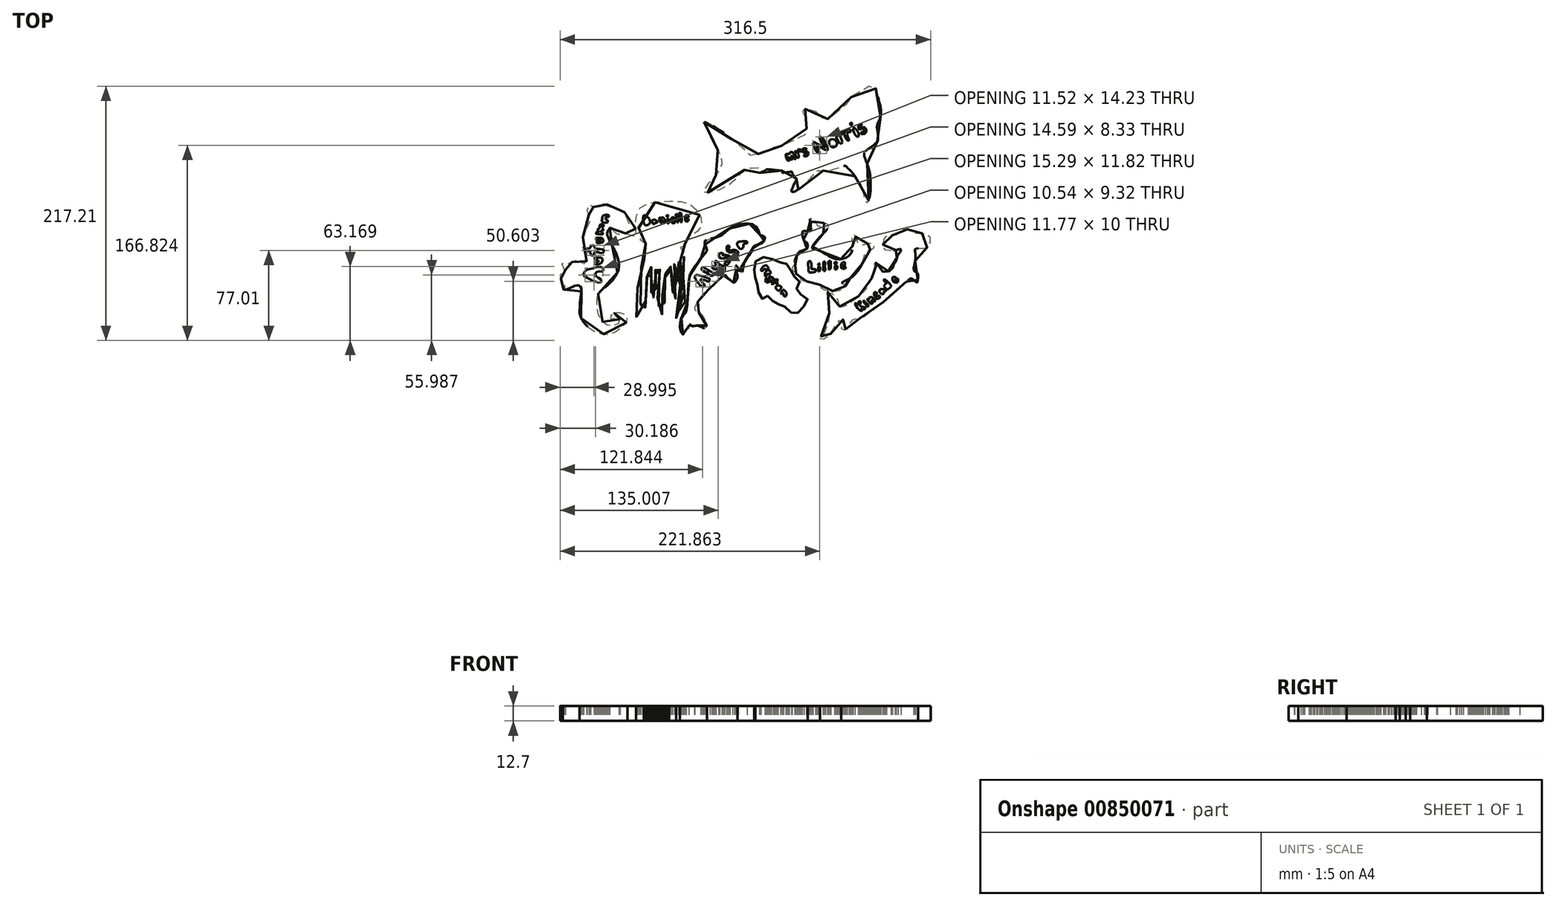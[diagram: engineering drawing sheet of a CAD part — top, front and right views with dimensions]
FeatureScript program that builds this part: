
annotation { "Feature Type Name" : "Feature", "Feature Type Description" : "" }
export const myFeature = defineFeature(function(context is Context, id is Id, definition is map)
    precondition{}
    {
        {
            var Q0;
            Q0=qCreatedBy(makeId("Top.planeOp"),FACE);
            var sketch = newSketch(context, id + "F0", { "sketchPlane" : qUnion([Q0])});
            skFitSpline(sketch, "E0", {"points": [v(-59.86, -6.15) * mm, v(-60.63, -4.76) * mm, v(-62.85, -4.35) * mm, v(-64.45, -3.65) * mm, v(-64.24, -1.7) * mm, v(-62.57, 0) * mm, v(-63.47, 2.6) * mm, v(-65.98, 7.6) * mm, v(-68.13, 12.13) * mm, v(-68.27, 15.81) * mm, v(-64.02, 25.07) * mm, v(-53.18, 29.24) * mm, v(-34.55, 30.36) * mm, v(-21.77, 27.58) * mm, v(-13.98, 18.68) * mm, v(-11.76, 10.34) * mm, v(-16.76, 3.39) * mm, v(-25.94, -2.17) * mm, v(-26.21, -5.5) * mm, v(-28.44, -8.57) * mm, v(-30.38, -9.12) * mm, v(-27.6, -11.9) * mm, v(-27.88, -14.68) * mm, v(-27.05, -18.3) * mm, v(-30.1, -19.97) * mm, v(-28.44, -25.8) * mm, v(-27.05, -32.2) * mm, v(-28.16, -37.76) * mm, v(-25.94, -43.87) * mm, v(-27.05, -48.32) * mm, v(-26.21, -54.72) * mm, v(-28.72, -61.95) * mm, v(-30.94, -67.78) * mm, v(-33.72, -70.56) * mm, v(-32.05, -62.22) * mm, v(-29.83, -57.22) * mm, v(-30.38, -50.27) * mm, v(-29, -44.7) * mm, v(-31.22, -38.04) * mm, v(-30.1, -34.14) * mm, v(-31.5, -28.58) * mm, v(-32.33, -20.52) * mm, v(-34.83, -20.8) * mm, v(-34, -29.97) * mm, v(-32.05, -34.14) * mm, v(-33.72, -38.04) * mm, v(-32.05, -45.26) * mm, v(-35.67, -54.16) * mm, v(-37.33, -43.6) * mm, v(-39.84, -36.92) * mm, v(-37.06, -32.2) * mm, v(-38.45, -26.92) * mm, v(-38.72, -21.08) * mm, v(-42.62, -21.08) * mm, v(-41.96, -25.83) * mm, v(-42.72, -30.28) * mm, v(-43.28, -36.53) * mm, v(-42.65, -40.84) * mm, v(-43.35, -44.6) * mm, v(-45.3, -48.35) * mm, v(-45.7, -51.75) * mm, v(-44.18, -55.16) * mm, v(-43.83, -59.12) * mm, v(-45.36, -61.13) * mm, v(-45.78, -66.83) * mm, v(-45.7, -67.53) * mm, v(-47.93, -65.24) * mm, v(-48.07, -61) * mm, v(-49.6, -57.1) * mm, v(-49.25, -50.78) * mm, v(-47.38, -43.97) * mm, v(-48.21, -34.86) * mm, v(-47.52, -27.63) * mm, v(-45.7, -22.35) * mm, v(-48.7, -21.17) * mm, v(-48.7, -24.5) * mm, v(-51.27, -27.56) * mm, v(-51.69, -30.9) * mm, v(-50.64, -33.4) * mm, v(-52.03, -37.02) * mm, v(-52.1, -39.24) * mm, v(-50.92, -44.1) * mm, v(-52.94, -48.14) * mm, v(-53.35, -51.54) * mm, v(-53.63, -53.9) * mm, v(-55.65, -50.08) * mm, v(-55.02, -47.51) * mm, v(-57.18, -43.06) * mm, v(-55.16, -35.14) * mm, v(-55.79, -29.72) * mm, v(-54.81, -20.68) * mm, v(-57.32, -20.06) * mm, v(-58.5, -28.05) * mm, v(-58.85, -34.65) * mm, v(-60.37, -40.77) * mm, v(-61.28, -45.08) * mm, v(-59.96, -49.11) * mm, v(-59.89, -56.48) * mm, v(-60.93, -63.64) * mm, v(-63.5, -67.39) * mm, v(-67.17, -71.06) * mm, v(-66.98, -61.23) * mm, v(-64.42, -58.28) * mm, v(-66.2, -47.08) * mm, v(-66.39, -42.56) * mm, v(-64.03, -37.64) * mm, v(-63.83, -27.42) * mm, v(-61.28, -18.18) * mm, v(-65.6, -15.62) * mm, v(-64.42, -11.89) * mm, v(-65.01, -9.53) * mm, v(-59.86, -6.15) * mm]});
            skFitSpline(sketch, "E1", {"points": [v(-60.84, 10.3) * mm, v(-61.48, 18.1) * mm, v(-58.93, 17.3) * mm, v(-56.22, 13.96) * mm, v(-57.01, 10.45) * mm, v(-58.77, 9.81) * mm, v(-60.84, 10.3) * mm]});
            skFitSpline(sketch, "E2", {"points": [v(-52.86, 10.57) * mm, v(-54.3, 13.64) * mm, v(-52.87, 14.6) * mm, v(-51.12, 13.96) * mm, v(-50, 12.52) * mm, v(-50.5, 11.76) * mm, v(-51.63, 11.9) * mm, v(-52.86, 10.57) * mm]});
            skFitSpline(sketch, "E3", {"points": [v(-47.61, 12.36) * mm, v(-48.09, 16.19) * mm, v(-47.13, 16.19) * mm, v(-46.97, 15.4) * mm, v(-45.7, 16.5) * mm, v(-44.1, 15.4) * mm, v(-43.3, 12.84) * mm, v(-44.42, 12.2) * mm, v(-45.22, 13.8) * mm, v(-46.34, 13.96) * mm, v(-46.04, 12.16) * mm, v(-47.61, 12.36) * mm]});
            skFitSpline(sketch, "E4", {"points": [v(-40.96, 11.48) * mm, v(-41.41, 15.2) * mm, v(-40.4, 15.32) * mm, v(-40.23, 11.6) * mm, v(-40.96, 11.48) * mm]});
            skFitSpline(sketch, "E5", {"points": [v(-41.19, 17.06) * mm, v(-42.03, 17.46) * mm, v(-41.41, 18.36) * mm, v(-40.51, 17.9) * mm, v(-41.19, 17.06) * mm]});
            skFitSpline(sketch, "E6", {"points": [v(-36.8, 14.47) * mm, v(-35.33, 15.26) * mm, v(-36.68, 16.67) * mm, v(-38.15, 15.09) * mm, v(-37.75, 12.22) * mm, v(-35.27, 11.65) * mm, v(-35.05, 13.12) * mm, v(-36.74, 12.9) * mm, v(-36.8, 14.47) * mm]});
            skFitSpline(sketch, "E7", {"points": [v(-33.07, 12.44) * mm, v(-34.09, 18.98) * mm, v(-32.9, 18.98) * mm, v(-32.29, 12.55) * mm, v(-33.07, 12.44) * mm]});
            skFitSpline(sketch, "E8", {"points": [v(-29.98, 12.5) * mm, v(-31.33, 19.94) * mm, v(-29.92, 20.27) * mm, v(-29.24, 16.39) * mm, v(-29.02, 12.67) * mm, v(-29.98, 12.5) * mm]});
            skFitSpline(sketch, "E9", {"points": [v(-24, 15.43) * mm, v(-24.4, 14.53) * mm, v(-25.19, 14.7) * mm, v(-25.13, 15.77) * mm, v(-24.34, 16.16) * mm, v(-23.04, 17.12) * mm, v(-24.23, 18.53) * mm, v(-25.97, 17.9) * mm, v(-26.26, 16.16) * mm, v(-26.09, 13.96) * mm, v(-24.45, 12.9) * mm, v(-23.44, 13.85) * mm, v(-23.21, 15.09) * mm, v(-24, 15.43) * mm]});
            skFitSpline(sketch, "E10", {"points": [v(-76.91, 2.77) * mm, v(-70.73, -0.55) * mm, v(-67.44, 0.8) * mm, v(-66.9, 3.47) * mm, v(-68.38, 6.96) * mm, v(-72.8, 8.37) * mm, v(-73.88, 10.44) * mm, v(-75.62, 14.93) * mm, v(-78.23, 21.03) * mm, v(-79.9, 21.43) * mm, v(-81.72, 22.5) * mm, v(-92.04, 25.05) * mm, v(-92.17, 25.99) * mm, v(-93.72, 28.05) * mm, v(-95.45, 27.44) * mm, v(-96.45, 28.31) * mm, v(-97.73, 29.52) * mm, v(-103.62, 24.9) * mm, v(-104.9, 25.63) * mm, v(-107.64, 27.44) * mm, v(-108.25, 26.3) * mm, v(-107.44, 23.49) * mm, v(-109.79, 22.75) * mm, v(-107.1, 15.45) * mm, v(-108.78, 11.36) * mm, v(-112.47, 2.51) * mm, v(-113.54, 0) * mm, v(-114.08, -8.68) * mm, v(-112, -15.31) * mm, v(-110.37, -20.12) * mm, v(-111.13, -22.06) * mm, v(-113.26, -23.77) * mm, v(-117.62, -21.97) * mm, v(-120.27, -20.03) * mm, v(-122.6, -21.54) * mm, v(-127.38, -22.82) * mm, v(-130.56, -21.92) * mm, v(-131.74, -22.87) * mm, v(-129.28, -27.23) * mm, v(-128.47, -28.98) * mm, v(-130.27, -29.79) * mm, v(-132.36, -30.07) * mm, v(-132.8, -32.58) * mm, v(-131.31, -34.15) * mm, v(-131.79, -35.52) * mm, v(-132.8, -36.47) * mm, v(-132.45, -38.8) * mm, v(-129.13, -41.16) * mm, v(-129.47, -42.44) * mm, v(-130.7, -44.05) * mm, v(-129.99, -45.28) * mm, v(-124.25, -43.67) * mm, v(-118.28, -41.54) * mm, v(-115.16, -43.3) * mm, v(-115.53, -51.73) * mm, v(-116.06, -59.3) * mm, v(-116.06, -66.6) * mm, v(-113.12, -72.67) * mm, v(-106.1, -79.54) * mm, v(-97.48, -83.1) * mm, v(-89, -83.05) * mm, v(-82.8, -79.16) * mm, v(-77, -73.95) * mm, v(-75.5, -70.59) * mm, v(-76.35, -67.46) * mm, v(-81.27, -65.28) * mm, v(-86.3, -65.09) * mm, v(-89.38, -67.41) * mm, v(-90.42, -70.16) * mm, v(-86.63, -69.73) * mm, v(-83.74, -69.21) * mm, v(-81.9, -71.53) * mm, v(-84.4, -74.9) * mm, v(-89.05, -76.37) * mm, v(-95.2, -74.24) * mm, v(-100.23, -66.37) * mm, v(-101.56, -57.22) * mm, v(-100.56, -49.03) * mm, v(-94.26, -43) * mm, v(-87.24, -36.18) * mm, v(-82.93, -27.47) * mm, v(-83.36, -19.22) * mm, v(-86.44, -11.6) * mm, v(-90.23, -4.44) * mm, v(-92.32, 0.54) * mm, v(-92.79, 3.15) * mm, v(-91.46, 6.23) * mm, v(-90.14, 7.65) * mm, v(-87.72, 5.75) * mm, v(-85.3, 3) * mm, v(-79.9, 2.3) * mm, v(-76.91, 2.77) * mm]});
            skFitSpline(sketch, "E11", {"points": [v(-97.57, 12.86) * mm, v(-95.35, 12.15) * mm, v(-93.36, 11.96) * mm, v(-92.46, 12.43) * mm, v(-92.08, 13.48) * mm, v(-93.12, 14.28) * mm, v(-94.02, 14.85) * mm, v(-94.21, 15.85) * mm, v(-93.83, 16.56) * mm, v(-93.26, 16.8) * mm, v(-92.22, 16.84) * mm, v(-91.7, 16.84) * mm, v(-91.27, 17.36) * mm, v(-91.32, 18.26) * mm, v(-92.36, 18.5) * mm, v(-94.3, 18.5) * mm, v(-95.58, 18.07) * mm, v(-96.4, 17.79) * mm, v(-96.96, 16.46) * mm, v(-96.96, 15.23) * mm, v(-97.43, 13.95) * mm, v(-97.57, 12.86) * mm]});
            skFitSpline(sketch, "E12", {"points": [v(-96.25, 6.89) * mm, v(-96.63, 7.74) * mm, v(-97.24, 7.98) * mm, v(-97.2, 8.55) * mm, v(-96.72, 8.93) * mm, v(-96.2, 8.93) * mm, v(-95.82, 8.88) * mm, v(-95.54, 9.26) * mm, v(-95.44, 9.97) * mm, v(-95.68, 10.25) * mm, v(-97.3, 10.54) * mm, v(-98.95, 10.2) * mm, v(-99.28, 8.26) * mm, v(-99.23, 7.27) * mm, v(-100.09, 6.84) * mm, v(-100.9, 6.32) * mm, v(-101.03, 5.52) * mm, v(-100.37, 4.62) * mm, v(-100, 4.14) * mm, v(-100.84, 3.86) * mm, v(-101.84, 4) * mm, v(-102.17, 3.62) * mm, v(-102.31, 2.9) * mm, v(-102.03, 2.39) * mm, v(-100.7, 2.06) * mm, v(-99.85, 2) * mm, v(-98.71, 2) * mm, v(-98.14, 1.96) * mm, v(-96.4, 1.91) * mm, v(-96.44, 3.24) * mm, v(-97, 3.8) * mm, v(-98.2, 4.28) * mm, v(-98.33, 4.76) * mm, v(-97.62, 5.28) * mm, v(-96.3, 5.14) * mm, v(-95.87, 6.23) * mm, v(-96.25, 6.89) * mm]});
            skFitSpline(sketch, "E13", {"points": [v(-101.98, -1.07) * mm, v(-99.23, -1.12) * mm, v(-97.39, -1.17) * mm, v(-96.2, -2.3) * mm, v(-96.06, -3.72) * mm, v(-97.05, -4.96) * mm, v(-98.66, -5.38) * mm, v(-100.56, -5.57) * mm, v(-101.32, -5.53) * mm, v(-101.7, -4.44) * mm, v(-101.08, -3.72) * mm, v(-99.38, -3.72) * mm, v(-98.29, -3.58) * mm, v(-98, -2.97) * mm, v(-98.29, -2.78) * mm, v(-99.94, -2.63) * mm, v(-101.18, -2.73) * mm, v(-102.12, -3.06) * mm, v(-102.46, -2.16) * mm, v(-101.98, -1.07) * mm]});
            skFitSpline(sketch, "E14", {"points": [v(-104.02, -15.86) * mm, v(-103.92, -14.24) * mm, v(-103.5, -13.1) * mm, v(-101.65, -13.25) * mm, v(-99.75, -13.58) * mm, v(-97.48, -14) * mm, v(-96.44, -13.77) * mm, v(-95.58, -12.92) * mm, v(-95.58, -11.92) * mm, v(-96.2, -10.97) * mm, v(-99.23, -10.55) * mm, v(-100.99, -10.4) * mm, v(-102.98, -10.12) * mm, v(-103.78, -8.89) * mm, v(-103.64, -7.66) * mm, v(-105.1, -7.47) * mm, v(-106.67, -7.37) * mm, v(-107.24, -8.89) * mm, v(-107, -9.7) * mm, v(-108.05, -10.17) * mm, v(-109.33, -9.93) * mm, v(-110.27, -9.98) * mm, v(-110.32, -11.07) * mm, v(-109.66, -12.2) * mm, v(-108.85, -12.59) * mm, v(-107.57, -12.54) * mm, v(-106.96, -12.59) * mm, v(-106.96, -13.63) * mm, v(-107.05, -14.72) * mm, v(-107, -15.57) * mm, v(-105.96, -16.05) * mm, v(-104.02, -15.86) * mm]});
            skFitSpline(sketch, "E15", {"points": [v(-103.12, -19.84) * mm, v(-101.7, -20.07) * mm, v(-100.42, -20.17) * mm, v(-100.32, -20.69) * mm, v(-100.42, -21.5) * mm, v(-101.5, -21.64) * mm, v(-102.65, -21.83) * mm, v(-103.02, -22.2) * mm, v(-102.98, -23.01) * mm, v(-102.17, -23.58) * mm, v(-100.23, -23.72) * mm, v(-98.43, -22.96) * mm, v(-97.48, -22.06) * mm, v(-96.86, -21.02) * mm, v(-96.67, -19.6) * mm, v(-97, -18.7) * mm, v(-97.62, -17.99) * mm, v(-98.85, -17.9) * mm, v(-101.03, -17.9) * mm, v(-101.93, -17.99) * mm, v(-103.07, -18.04) * mm, v(-103.6, -18.6) * mm, v(-103.5, -19.5) * mm, v(-103.12, -19.84) * mm]});
            skFitSpline(sketch, "E16", {"points": [v(-102.27, -33.86) * mm, v(-103.17, -32.68) * mm, v(-102.98, -31.4) * mm, v(-102.08, -30.5) * mm, v(-100.6, -29.74) * mm, v(-98.85, -29.79) * mm, v(-97.3, -29.83) * mm, v(-96.58, -29.64) * mm, v(-96.01, -28.6) * mm, v(-96.01, -27.6) * mm, v(-96.96, -26.66) * mm, v(-97.86, -26.1) * mm, v(-99.8, -25.8) * mm, v(-102.83, -26.56) * mm, v(-105.82, -27.23) * mm, v(-108.05, -27.7) * mm, v(-108.85, -27.84) * mm, v(-110.04, -28.22) * mm, v(-111.27, -29.36) * mm, v(-112.5, -30.36) * mm, v(-112.88, -31.5) * mm, v(-112.83, -32.91) * mm, v(-111.32, -34.53) * mm, v(-109.56, -35.28) * mm, v(-108.05, -36.23) * mm, v(-105.1, -37.7) * mm, v(-102.93, -38.27) * mm, v(-101.32, -39.07) * mm, v(-99.9, -39.26) * mm, v(-98.48, -39.26) * mm, v(-97.67, -38.17) * mm, v(-98, -36.8) * mm, v(-99.66, -35.38) * mm, v(-101.89, -34.34) * mm, v(-102.27, -33.86) * mm]});
            skFitSpline(sketch, "E17", {"points": [v(-28.23, -83.72) * mm, v(-30.3, -79.34) * mm, v(-30.38, -72.96) * mm, v(-28.4, -67.78) * mm, v(-25.68, -64.75) * mm, v(-24.57, -59.26) * mm, v(-23.45, -44.27) * mm, v(-22.17, -32.96) * mm, v(-18.67, -26.9) * mm, v(-12.77, -18.61) * mm, v(-7.6, -12.4) * mm, v(-7.6, -11.12) * mm, v(-8.55, -8.01) * mm, v(-9.66, -4.35) * mm, v(-8.79, -3.47) * mm, v(-4.8, -1.96) * mm, v(3.09, 0) * mm, v(5.48, 1.4) * mm, v(9.54, 5.3) * mm, v(17.11, 9.84) * mm, v(24.92, 11.2) * mm, v(32.42, 10.4) * mm, v(35.28, 7.29) * mm, v(37.68, 2.19) * mm, v(37.91, 1.07) * mm, v(39.83, 0.91) * mm, v(41.74, 0) * mm, v(42.06, -2.12) * mm, v(40.54, -4.5) * mm, v(37.52, -6.66) * mm, v(33.37, -7.22) * mm, v(31.38, -10.64) * mm, v(27.95, -16.54) * mm, v(25.16, -19.97) * mm, v(24.05, -23.31) * mm, v(22.85, -29.6) * mm, v(22.3, -30.49) * mm, v(21.1, -30) * mm, v(18, -25.3) * mm, v(17.03, -24.59) * mm, v(16.24, -25.62) * mm, v(16.4, -27.22) * mm, v(18.39, -32.24) * mm, v(18.39, -35.35) * mm, v(15.84, -39.07) * mm, v(14.88, -39.07) * mm, v(12.1, -36.7) * mm, v(9.46, -34.23) * mm, v(7.71, -32.8) * mm, v(3.89, -35.75) * mm, v(-2.49, -41.24) * mm, v(-8.15, -47.06) * mm, v(-11.5, -49.77) * mm, v(-14.68, -54.4) * mm, v(-17.23, -58.62) * mm, v(-18.19, -61.8) * mm, v(-16.44, -64.04) * mm, v(-12.7, -66.03) * mm, v(-9.1, -71.05) * mm, v(-7.9, -74.8) * mm, v(-7.75, -77.03) * mm, v(-9.34, -78.14) * mm, v(-12.13, -77.27) * mm, v(-14.28, -76.39) * mm, v(-16.28, -76) * mm, v(-19.07, -76.47) * mm, v(-20.26, -76.47) * mm, v(-22.1, -74.96) * mm, v(-22.9, -76) * mm, v(-23.6, -78.7) * mm, v(-25.52, -79.66) * mm, v(-26.88, -81.49) * mm, v(-28.23, -83.72) * mm]});
            skFitSpline(sketch, "E18", {"points": [v(-10.9, -43.1) * mm, v(-17.6, -35.53) * mm, v(-17.8, -33.98) * mm, v(-16.93, -33.05) * mm, v(-16.13, -32.64) * mm, v(-5.14, -36.33) * mm, v(-5.2, -37.2) * mm, v(-5.68, -38.07) * mm, v(-6.68, -38.34) * mm, v(-12.31, -36.2) * mm, v(-12.98, -36.8) * mm, v(-12.38, -38.2) * mm, v(-10.3, -40.42) * mm, v(-9.36, -41.82) * mm, v(-10.9, -43.1) * mm]});
            skFitSpline(sketch, "E19", {"points": [v(-2.93, -33.58) * mm, v(-7.55, -31.1) * mm, v(-12.1, -28.02) * mm, v(-11.7, -26.48) * mm, v(-11.1, -26.08) * mm, v(-6.15, -28.9) * mm, v(-2, -31.57) * mm, v(-2.33, -32.71) * mm, v(-2.93, -33.58) * mm]});
            skFitSpline(sketch, "E20", {"points": [v(-3.26, -26.55) * mm, v(-1.39, -27.68) * mm, v(0, -28.15) * mm, v(2.23, -26.34) * mm, v(2.77, -25.2) * mm, v(5.31, -26.68) * mm, v(5.25, -28.29) * mm, v(4.04, -29.1) * mm, v(3.24, -29.96) * mm, v(4.3, -31.1) * mm, v(6.19, -30.7) * mm, v(7.4, -29.1) * mm, v(7.6, -25.88) * mm, v(4.04, -24.33) * mm, v(0.9, -20.85) * mm, v(0, -20.65) * mm, v(-0.92, -22.26) * mm, v(0, -23.46) * mm, v(0, -24.8) * mm, v(-1.25, -25.74) * mm, v(-2.8, -24.94) * mm, v(-3.26, -26.55) * mm]});
            skFitSpline(sketch, "E21", {"points": [v(6.39, -14.75) * mm, v(5.72, -15.96) * mm, v(7.06, -15.76) * mm, v(9.34, -15.62) * mm, v(11.68, -16.36) * mm, v(12.28, -18.57) * mm, v(11.81, -21.32) * mm, v(9.74, -24.33) * mm, v(8.06, -24.33) * mm, v(7.73, -22.19) * mm, v(9.54, -21.25) * mm, v(10.27, -18.64) * mm, v(9.27, -17.3) * mm, v(7.4, -18.37) * mm, v(4.71, -18.7) * mm, v(2.77, -17.36) * mm, v(2.77, -14.95) * mm, v(4.91, -13.81) * mm, v(6.39, -14.75) * mm]});
            skFitSpline(sketch, "E22", {"points": [v(11.88, -8.12) * mm, v(11.08, -10) * mm, v(11.35, -11.47) * mm, v(13.42, -11.6) * mm, v(15.5, -11.07) * mm, v(18.25, -12) * mm, v(18.99, -14.75) * mm, v(16.9, -17.3) * mm, v(14.96, -17.83) * mm, v(14.5, -16.3) * mm, v(15.77, -14.88) * mm, v(16.64, -13.48) * mm, v(15.43, -12.8) * mm, v(13.36, -13.41) * mm, v(10.27, -13.08) * mm, v(9.27, -10.2) * mm, v(9.74, -7.71) * mm, v(11.88, -8.12) * mm]});
            skFitSpline(sketch, "E23", {"points": [v(21.46, -10.66) * mm, v(23.4, -8.99) * mm, v(23.94, -6.3) * mm, v(25.35, -5.9) * mm, v(26.83, -5.5) * mm, v(26.42, -4.16) * mm, v(22.67, -4.03) * mm, v(19.39, -4.43) * mm, v(18.25, -6.1) * mm, v(19.05, -8.45) * mm, v(21.46, -10.66) * mm]});
            skFitSpline(sketch, "E24", {"points": [v(44.3, -50.42) * mm, v(42.5, -52.56) * mm, v(39.22, -52.8) * mm, v(36.97, -50.2) * mm, v(36.3, -44.68) * mm, v(35.28, -40.05) * mm, v(34.04, -38.14) * mm, v(33.81, -34.23) * mm, v(32.91, -29.35) * mm, v(33.02, -24.33) * mm, v(35.17, -19.54) * mm, v(41.25, -17.4) * mm, v(46.21, -18.3) * mm, v(52.3, -20.78) * mm, v(55.9, -22.13) * mm, v(58.27, -22.13) * mm, v(62.1, -25.2) * mm, v(64.36, -28.9) * mm, v(65.03, -31.26) * mm, v(67.62, -34.23) * mm, v(71.12, -36.7) * mm, v(71.23, -41.07) * mm, v(69.1, -44.56) * mm, v(69.43, -46.6) * mm, v(74.16, -50.04) * mm, v(78, -52.8) * mm, v(78.1, -55.6) * mm, v(74.27, -60.8) * mm, v(70.44, -64.74) * mm, v(67.62, -66.43) * mm, v(63, -63.72) * mm, v(59.28, -60.57) * mm, v(56.24, -57.1) * mm, v(52.86, -58.09) * mm, v(49.37, -56.17) * mm, v(47.56, -52.68) * mm, v(44.3, -50.42) * mm]});
            skFitSpline(sketch, "E25", {"points": [v(38.55, -28.45) * mm, v(42.76, -24.33) * mm, v(44.28, -25.62) * mm, v(45.07, -27.43) * mm, v(43.04, -28.05) * mm, v(41.4, -27.6) * mm, v(39.77, -29.12) * mm, v(38.55, -28.45) * mm]});
            skFitSpline(sketch, "E26", {"points": [v(42.2, -33.63) * mm, v(42.08, -31.55) * mm, v(42.76, -29.69) * mm, v(44.16, -28.73) * mm, v(46.02, -29.18) * mm, v(46.87, -30.7) * mm, v(46.36, -31.94) * mm, v(44.78, -31.77) * mm, v(43.88, -31.71) * mm, v(43.54, -32.22) * mm, v(43.71, -33.12) * mm, v(43.15, -33.97) * mm, v(42.2, -33.63) * mm]});
            skFitSpline(sketch, "E27", {"points": [v(47.04, -33.52) * mm, v(46.93, -34.42) * mm, v(47.43, -35.1) * mm, v(48.1, -34.76) * mm, v(48.73, -34.81) * mm, v(48.9, -35.43) * mm, v(48.79, -36.4) * mm, v(46.87, -37.91) * mm, v(45.3, -38.93) * mm, v(43.49, -39.04) * mm, v(42.53, -38.3) * mm, v(42.47, -36.62) * mm, v(43.04, -35.77) * mm, v(43.94, -35.77) * mm, v(44.1, -36.62) * mm, v(44.28, -37.58) * mm, v(45.46, -37.18) * mm, v(46.08, -36.56) * mm, v(46.02, -35.72) * mm, v(45.46, -35.38) * mm, v(45.35, -34.48) * mm, v(47.04, -33.52) * mm]});
            skFitSpline(sketch, "E28", {"points": [v(47.43, -40) * mm, v(48.73, -39.1) * mm, v(50.08, -38.3) * mm, v(49.3, -36.9) * mm, v(50.03, -36.17) * mm, v(51.15, -37.01) * mm, v(52.34, -36.34) * mm, v(53.07, -37.07) * mm, v(52, -37.97) * mm, v(52.45, -38.87) * mm, v(52.9, -39.6) * mm, v(52.11, -40.11) * mm, v(51.1, -39.6) * mm, v(50.53, -39.1) * mm, v(50.2, -39.6) * mm, v(48.5, -40.56) * mm, v(47.43, -40) * mm]});
            skFitSpline(sketch, "E29", {"points": [v(51.94, -45.07) * mm, v(51.43, -42.87) * mm, v(53.12, -41.63) * mm, v(54.98, -42.14) * mm, v(56.17, -43.27) * mm, v(55.27, -45.18) * mm, v(54.14, -46.25) * mm, v(51.94, -45.07) * mm]});
            skFitSpline(sketch, "E30", {"points": [v(55.43, -48.56) * mm, v(56.67, -46.7) * mm, v(57.69, -45.35) * mm, v(59.1, -46.3) * mm, v(60.11, -47.6) * mm, v(60.4, -49.8) * mm, v(59.21, -51.04) * mm, v(57.97, -50.54) * mm, v(57.8, -48.68) * mm, v(57.13, -48.17) * mm, v(56.22, -48.96) * mm, v(55.43, -48.56) * mm]});
            skFitSpline(sketch, "E31", {"points": [v(67.65, -24.53) * mm, v(65.57, -25.85) * mm, v(65.47, -27.84) * mm, v(67.75, -31.07) * mm, v(71.35, -34.48) * mm, v(72.96, -36.85) * mm, v(78.74, -38.36) * mm, v(83.76, -39.88) * mm, v(87.93, -40.07) * mm, v(89.73, -43) * mm, v(94.28, -45.66) * mm, v(101.96, -46.51) * mm, v(107.83, -45.1) * mm, v(110.77, -42.53) * mm, v(109.26, -40.83) * mm, v(107.93, -39.31) * mm, v(113.9, -36.18) * mm, v(121.58, -28.98) * mm, v(125.56, -21.59) * mm, v(128.02, -13.63) * mm, v(132.2, -11.07) * mm, v(135.6, -8.51) * mm, v(133.61, -5.76) * mm, v(126.5, -7) * mm, v(121.48, -4.9) * mm, v(118.73, 1.16) * mm, v(116.55, 0.87) * mm, v(116.74, -6.33) * mm, v(114.85, -15.14) * mm, v(107.36, -19.22) * mm, v(97.98, -17.42) * mm, v(89.73, -12.4) * mm, v(83.86, -10.79) * mm, v(82.44, -10.12) * mm, v(82.72, -8.32) * mm, v(85.56, -4.06) * mm, v(92.39, 3.24) * mm, v(96.18, 8.36) * mm, v(94.76, 10.73) * mm, v(90.68, 11.1) * mm, v(88.88, 8.26) * mm, v(85.75, 11.49) * mm, v(84.43, 14.33) * mm, v(82.62, 15.18) * mm, v(80.44, 15.09) * mm, v(80.82, 11.49) * mm, v(81.1, 7.7) * mm, v(81.01, 5.04) * mm, v(77.03, 4.85) * mm, v(74.16, 4.38) * mm, v(74.16, 0) * mm, v(76.27, -4.06) * mm, v(77.89, -5.2) * mm, v(78.64, -8.8) * mm, v(77.03, -10.79) * mm, v(72.58, -12.3) * mm, v(70.68, -13.63) * mm, v(68.4, -18.18) * mm, v(67.37, -21.12) * mm, v(68.03, -22.73) * mm, v(67.65, -24.53) * mm]});
            skFitSpline(sketch, "E32", {"points": [v(79.5, -30.12) * mm, v(79.02, -24.72) * mm, v(79.12, -21.5) * mm, v(80.44, -20.83) * mm, v(81.4, -21.87) * mm, v(81.68, -25.2) * mm, v(81.68, -27.18) * mm, v(82.06, -27.75) * mm, v(83.2, -27.75) * mm, v(84.9, -27.65) * mm, v(85.28, -28.8) * mm, v(85.09, -29.83) * mm, v(83.48, -30.5) * mm, v(80.63, -30.4) * mm, v(79.5, -30.12) * mm]});
            skFitSpline(sketch, "E33", {"points": [v(87.55, -29.46) * mm, v(87.36, -27.37) * mm, v(87.65, -26.04) * mm, v(89.07, -25.95) * mm, v(89.26, -27.37) * mm, v(89.16, -28.32) * mm, v(88.6, -29.36) * mm, v(87.55, -29.46) * mm]});
            skFitSpline(sketch, "E34", {"points": [v(87.93, -24.53) * mm, v(87.46, -23.86) * mm, v(88.22, -23.01) * mm, v(88.78, -23.4) * mm, v(87.93, -24.53) * mm]});
            skFitSpline(sketch, "E35", {"points": [v(92.1, -29.27) * mm, v(91.91, -25.76) * mm, v(91.91, -23.77) * mm, v(92, -21.97) * mm, v(92.86, -21.21) * mm, v(93.33, -22.44) * mm, v(93.24, -25.1) * mm, v(93.43, -27.18) * mm, v(93.62, -28.8) * mm, v(92.1, -29.27) * mm]});
            skFitSpline(sketch, "E36", {"points": [v(96.65, -28.03) * mm, v(96.65, -25.38) * mm, v(96.18, -22.92) * mm, v(96.18, -21.3) * mm, v(97.6, -20.64) * mm, v(98.26, -22.25) * mm, v(98.26, -24.72) * mm, v(98.17, -26.8) * mm, v(96.65, -28.03) * mm]});
            skFitSpline(sketch, "E37", {"points": [v(101.77, -27.94) * mm, v(101.77, -26.23) * mm, v(101.96, -25) * mm, v(103.85, -25) * mm, v(103.76, -26.7) * mm, v(103.2, -27.75) * mm, v(101.77, -27.94) * mm]});
            skFitSpline(sketch, "E38", {"points": [v(101.86, -23.4) * mm, v(101.39, -22.44) * mm, v(102.34, -21.59) * mm, v(103.47, -22.44) * mm, v(101.86, -23.4) * mm]});
            skFitSpline(sketch, "E39", {"points": [v(108.6, -27.56) * mm, v(107.08, -26.61) * mm, v(107.08, -25.29) * mm, v(107.08, -23.77) * mm, v(108.12, -22.25) * mm, v(109.63, -21.68) * mm, v(110.4, -22.73) * mm, v(110.01, -24.43) * mm, v(108.69, -24.72) * mm, v(108.4, -25.48) * mm, v(108.88, -26.33) * mm, v(110.1, -25.76) * mm, v(110.68, -25.76) * mm, v(110.77, -26.9) * mm, v(109.92, -27.37) * mm, v(108.6, -27.56) * mm]});
            skPoint(sketch, "E40.41.internal.snap0", {"position": v(172, 2.77) * mm});
            skFitSpline(sketch, "E40", {"points": [v(105.94, -59.88) * mm, v(104.7, -55.14) * mm, v(101.96, -50.04) * mm, v(95.6, -47.27) * mm, v(95.6, -48.22) * mm, v(96.56, -52.96) * mm, v(97.12, -63.29) * mm, v(95.7, -74.95) * mm, v(92.2, -83.29) * mm, v(89.26, -86.32) * mm, v(89.35, -88.59) * mm, v(91.91, -87.74) * mm, v(96.56, -84.61) * mm, v(100.63, -79.3) * mm, v(104.04, -72.77) * mm, v(106.98, -70.97) * mm, v(109.26, -71.25) * mm, v(107.83, -75.99) * mm, v(107.36, -79.78) * mm, v(108.78, -80.25) * mm, v(113.05, -76.94) * mm, v(115.32, -73.05) * mm, v(116.65, -71.16) * mm, v(126.6, -68.4) * mm, v(135.89, -61.01) * mm, v(143.94, -55.14) * mm, v(153.23, -46.51) * mm, v(163.84, -37.6) * mm, v(166.78, -35.71) * mm, v(169.63, -37.42) * mm, v(172, -39.03) * mm, v(172.75, -34.95) * mm, v(172, -30.69) * mm, v(169.34, -29.17) * mm, v(170.76, -16.38) * mm, v(170.48, -10.7) * mm, v(178.63, -9.74) * mm, v(182.32, -7.18) * mm, v(183.37, -1.3) * mm, v(180.14, 1.82) * mm, v(172, 2.77) * mm, v(169.44, 2.77) * mm, v(167.92, 4.19) * mm, v(165.36, 5.7) * mm, v(159.86, 6.08) * mm, v(156.93, 4.1) * mm, v(154.46, 1.63) * mm, v(150.86, 1.35) * mm, v(148.78, 1.25) * mm, v(145.36, 0) * mm, v(143.47, -2.45) * mm, v(142.8, -7.09) * mm, v(143.37, -10.4) * mm, v(146.4, -11.45) * mm, v(151.8, -11.73) * mm, v(155.6, -11.07) * mm, v(158.06, -10.6) * mm, v(157.68, -12.68) * mm, v(155.22, -16.28) * mm, v(154.46, -19.7) * mm, v(152.19, -23.77) * mm, v(151.24, -25.95) * mm, v(148.5, -29.17) * mm, v(145.36, -29.74) * mm, v(142.9, -29.83) * mm, v(140.15, -25.85) * mm, v(137.97, -23.2) * mm, v(135.8, -22.25) * mm, v(135.98, -28.6) * mm, v(134.28, -33.44) * mm, v(131.81, -38.36) * mm, v(129.44, -42.91) * mm, v(123.1, -50.04) * mm, v(119.59, -52.96) * mm, v(112.57, -58.08) * mm, v(105.94, -59.88) * mm]});
            skFitSpline(sketch, "E41", {"points": [v(124.32, -63.86) * mm, v(121.3, -61.01) * mm, v(119.59, -58.74) * mm, v(118.92, -56.94) * mm, v(120.53, -57.22) * mm, v(121.3, -58.08) * mm, v(122.14, -57.41) * mm, v(121.95, -56.09) * mm, v(122.62, -55.04) * mm, v(123.95, -55.7) * mm, v(123.19, -57.7) * mm, v(123.47, -59.3) * mm, v(124.8, -59.69) * mm, v(126.7, -60.26) * mm, v(127.64, -60.54) * mm, v(127.36, -61.87) * mm, v(125.08, -62.15) * mm, v(124.04, -61.68) * mm, v(124.9, -63.1) * mm, v(124.32, -63.86) * mm]});
            skFitSpline(sketch, "E42", {"points": [v(126.6, -56.37) * mm, v(126.03, -55.42) * mm, v(126.7, -54.76) * mm, v(127.26, -55.42) * mm, v(126.6, -56.37) * mm]});
            skFitSpline(sketch, "E43", {"points": [v(129.92, -59.78) * mm, v(128.12, -58.46) * mm, v(127.64, -57.7) * mm, v(127.93, -56.66) * mm, v(128.97, -56.94) * mm, v(129.73, -57.89) * mm, v(130.3, -58.46) * mm, v(129.92, -59.78) * mm]});
            skFitSpline(sketch, "E44", {"points": [v(132.66, -57.41) * mm, v(131.05, -56) * mm, v(130.1, -54.95) * mm, v(129.63, -54.1) * mm, v(129.63, -53.34) * mm, v(131.24, -53.34) * mm, v(131.05, -52.2) * mm, v(131.9, -51.92) * mm, v(133.04, -51.54) * mm, v(133.9, -52.2) * mm, v(135.6, -53.72) * mm, v(136.27, -54.48) * mm, v(135.98, -55.23) * mm, v(134.18, -54.95) * mm, v(133.33, -54.29) * mm, v(132.76, -55.14) * mm, v(133.42, -55.8) * mm, v(134.09, -56.66) * mm, v(132.66, -57.41) * mm]});
            skFitSpline(sketch, "E45", {"points": [v(139.68, -50.21) * mm, v(138.54, -51.06) * mm, v(137.4, -51.06) * mm, v(136.77, -50.04) * mm, v(137.21, -48.88) * mm, v(137.97, -48.32) * mm, v(137.02, -47.65) * mm, v(135.98, -47.37) * mm, v(135.21, -48.92) * mm, v(135.32, -50.04) * mm, v(135.89, -51.54) * mm, v(136.74, -52.58) * mm, v(137.88, -53.15) * mm, v(139.58, -52.58) * mm, v(140.34, -51.82) * mm, v(139.68, -50.21) * mm]});
            skFitSpline(sketch, "E46", {"points": [v(142.42, -49.24) * mm, v(140.43, -47.97) * mm, v(139.91, -46.22) * mm, v(140.6, -44.86) * mm, v(142.26, -44.98) * mm, v(143.82, -45.02) * mm, v(144.81, -45.54) * mm, v(145.33, -46.45) * mm, v(144.22, -46.85) * mm, v(143.62, -46.97) * mm, v(143.74, -47.73) * mm, v(143.5, -48.45) * mm, v(142.42, -49.24) * mm]});
            skFitSpline(sketch, "E47", {"points": [v(147.25, -44.78) * mm, v(148.92, -43.66) * mm, v(149.8, -42.39) * mm, v(148.84, -40.52) * mm, v(146.89, -38.37) * mm, v(145.17, -36.93) * mm, v(144.22, -36.45) * mm, v(143.34, -37.17) * mm, v(143.94, -37.93) * mm, v(144.85, -39) * mm, v(145.81, -39.96) * mm, v(144.66, -40.68) * mm, v(143.86, -42.15) * mm, v(144.7, -43.43) * mm, v(146.33, -45.02) * mm, v(147.25, -44.78) * mm]});
            skFitSpline(sketch, "E48", {"points": [v(154.62, -36.05) * mm, v(154.34, -37.13) * mm, v(153.22, -37.17) * mm, v(153.42, -36.41) * mm, v(153.94, -35.66) * mm, v(153.86, -34.94) * mm, v(152.86, -34.46) * mm, v(151.3, -34.58) * mm, v(150.87, -35.7) * mm, v(150.91, -36.9) * mm, v(151.87, -38.4) * mm, v(153.34, -39) * mm, v(155.06, -39.08) * mm, v(155.77, -38.2) * mm, v(155.81, -36.85) * mm, v(155.45, -35.82) * mm, v(154.62, -36.05) * mm]});
            skSolve(sketch);
        }
        {
            var Q0;
            Q0 = qSketchRegion(id + "F0", true);
            extrude(context, id + "F1", {"entities" : qUnion([Q0]), "depth" : 12.7 * mm, "offsetDistance" : 25.4 * mm});
        }
        {
            var Q0;
            Q0=qCreatedBy(makeId("Top.planeOp"),FACE);
            var sketch = newSketch(context, id + "F2", { "sketchPlane" : qUnion([Q0])});
            skFitSpline(sketch, "E49", {"points": [v(-10.14, 98.08) * mm, v(-9.42, 96.35) * mm, v(-4.74, 87.5) * mm, v(-0.98, 80.98) * mm, v(1.57, 74.47) * mm, v(4.31, 68.16) * mm, v(5.33, 63.58) * mm, v(4.52, 59.61) * mm, v(1.77, 55.03) * mm, v(-1.9, 49.64) * mm, v(-6.57, 44.96) * mm, v(-9.73, 40.38) * mm, v(-10.65, 39.57) * mm, v(-10.65, 38.04) * mm, v(1.67, 39.87) * mm, v(13.47, 45.98) * mm, v(23.65, 56.25) * mm, v(27.1, 58.5) * mm, v(32.4, 58.8) * mm, v(37.6, 58.7) * mm, v(37.29, 57.78) * mm, v(37.29, 56.15) * mm, v(37.29, 54.73) * mm, v(38.5, 54.63) * mm, v(39.63, 55.54) * mm, v(41.56, 56.25) * mm, v(43.7, 57.48) * mm, v(44.71, 57.58) * mm, v(50.62, 56.97) * mm, v(57.03, 56.25) * mm, v(57.03, 55.95) * mm, v(57.03, 54.52) * mm, v(59.27, 54.93) * mm, v(65.17, 55.44) * mm, v(65.27, 55.03) * mm, v(66.29, 52.49) * mm, v(69.14, 49.54) * mm, v(69.44, 49.54) * mm, v(67.5, 46.18) * mm, v(65.37, 41.5) * mm, v(64.76, 38.85) * mm, v(66.6, 38.45) * mm, v(72.7, 41.9) * mm, v(80.74, 49.74) * mm, v(85.52, 55.13) * mm, v(87.45, 56.36) * mm, v(97.22, 56.97) * mm, v(110.45, 60.53) * mm, v(111.37, 60.02) * mm, v(117.07, 54.32) * mm, v(121.24, 47.8) * mm, v(125.2, 40.28) * mm, v(127.96, 30.5) * mm, v(129.58, 29.54) * mm, v(131.62, 35.3) * mm, v(132.33, 47.3) * mm, v(131.21, 55.85) * mm, v(128.57, 64.5) * mm, v(126.94, 68.87) * mm, v(126.73, 71.42) * mm, v(128.06, 73.15) * mm, v(136.8, 79.96) * mm, v(138.54, 82.81) * mm, v(138.34, 88.72) * mm, v(137.62, 93.9) * mm, v(138.74, 97.57) * mm, v(140.64, 102.45) * mm, v(140.64, 111.1) * mm, v(139.25, 116.1) * mm, v(138.44, 121.9) * mm, v(137.11, 126.17) * mm, v(133.76, 128.23) * mm, v(130.2, 128.23) * mm, v(126.02, 125.45) * mm, v(119, 121.38) * mm, v(114.42, 117.92) * mm, v(110.76, 112.43) * mm, v(105.87, 107.85) * mm, v(97.83, 102.45) * mm, v(93.66, 99.3) * mm, v(91.93, 100.83) * mm, v(87.96, 105.1) * mm, v(82.47, 108.46) * mm, v(75.45, 108.97) * mm, v(73.1, 108.36) * mm, v(74.84, 106.32) * mm, v(76.67, 103.17) * mm, v(77.48, 98.28) * mm, v(77.58, 92.58) * mm, v(76.67, 89.12) * mm, v(75.5, 86.38) * mm, v(68.42, 82.92) * mm, v(56.72, 77.83) * mm, v(52.14, 75.9) * mm, v(44.82, 75.9) * mm, v(44.71, 72.74) * mm, v(38.81, 71.11) * mm, v(34.54, 69.9) * mm, v(29.25, 69.48) * mm, v(23.04, 75.7) * mm, v(14.29, 82.71) * mm, v(9.3, 87.2) * mm, v(0, 93.1) * mm, v(-7.08, 97.47) * mm, v(-10.14, 98.08) * mm]});
            skFitSpline(sketch, "E50", {"points": [v(61.6, 64.8) * mm, v(59.77, 70.5) * mm, v(60.39, 70.8) * mm, v(61, 69.79) * mm, v(61.6, 71.1) * mm, v(63.03, 70.5) * mm, v(63.54, 72.13) * mm, v(65.37, 72.23) * mm, v(68.22, 66.63) * mm, v(67.5, 66.12) * mm, v(65.37, 69.07) * mm, v(64.46, 68.77) * mm, v(65.37, 66.33) * mm, v(64.05, 65.61) * mm, v(62.32, 68.06) * mm, v(61.5, 67.95) * mm, v(62.83, 65.2) * mm, v(61.6, 64.8) * mm]});
            skFitSpline(sketch, "E51", {"points": [v(69.85, 67.24) * mm, v(67.5, 72.53) * mm, v(68.42, 73.14) * mm, v(68.83, 72.33) * mm, v(69.54, 72.64) * mm, v(70.46, 74.57) * mm, v(72.7, 73.96) * mm, v(72.7, 72.74) * mm, v(71.17, 72.94) * mm, v(70.26, 71.41) * mm, v(71.07, 69.07) * mm, v(69.85, 67.24) * mm]});
            skFitSpline(sketch, "E52", {"points": [v(87.45, 71) * mm, v(83.08, 80.06) * mm, v(84, 80.78) * mm, v(92.95, 76.3) * mm, v(91.52, 79.35) * mm, v(88.68, 84.74) * mm, v(90, 85.25) * mm, v(95.8, 74.77) * mm, v(94.68, 73.96) * mm, v(86.23, 77.72) * mm, v(88.57, 72.02) * mm, v(87.45, 71) * mm]});
            skFitSpline(sketch, "E53", {"points": [v(97.12, 78.84) * mm, v(98.24, 83.12) * mm, v(103.43, 80.78) * mm, v(101.3, 76.5) * mm, v(97.12, 78.84) * mm]});
            skFitSpline(sketch, "E54", {"points": [v(106.48, 79.56) * mm, v(102.92, 86.37) * mm, v(103.53, 87.09) * mm, v(104.14, 86.37) * mm, v(105.16, 86.68) * mm, v(105.47, 89.12) * mm, v(107.6, 89.22) * mm, v(107.9, 87.5) * mm, v(106.38, 87.7) * mm, v(106.59, 85.05) * mm, v(108.01, 80.67) * mm, v(106.48, 79.56) * mm]});
            skFitSpline(sketch, "E55", {"points": [v(112.59, 82.1) * mm, v(109.44, 90.34) * mm, v(110.25, 90.75) * mm, v(111.06, 89.63) * mm, v(111.88, 91.66) * mm, v(115.13, 90.95) * mm, v(114.83, 89.32) * mm, v(113.2, 89.53) * mm, v(112.18, 87.19) * mm, v(113.81, 82.81) * mm, v(112.59, 82.1) * mm]});
            skFitSpline(sketch, "E56", {"points": [v(120.73, 85.46) * mm, v(117.27, 92.07) * mm, v(118.6, 92.78) * mm, v(122.26, 86.78) * mm, v(120.73, 85.46) * mm]});
            skFitSpline(sketch, "E57", {"points": [v(116.15, 95.23) * mm, v(114.83, 96.24) * mm, v(115.95, 97.47) * mm, v(116.15, 95.23) * mm]});
            skFitSpline(sketch, "E58", {"points": [v(125.31, 96.14) * mm, v(122.16, 95.33) * mm, v(122.46, 91.77) * mm, v(125.51, 92.17) * mm, v(126.94, 90.55) * mm, v(124.2, 89.12) * mm, v(124.6, 87.6) * mm, v(127.75, 88.51) * mm, v(128.57, 91.46) * mm, v(126.73, 93.5) * mm, v(123.48, 93.4) * mm, v(123.58, 94.72) * mm, v(125.31, 96.14) * mm]});
            skFitSpline(sketch, "E59", {"points": [v(77.79, 74.77) * mm, v(75.5, 75.6) * mm, v(73.82, 73.35) * mm, v(75.5, 71.62) * mm, v(77.07, 71.52) * mm, v(77.28, 70.4) * mm, v(75.5, 69.68) * mm, v(75.5, 68.77) * mm, v(78.5, 69.28) * mm, v(79.1, 71.31) * mm, v(77.89, 72.84) * mm, v(75.75, 73.14) * mm, v(75.5, 73.87) * mm, v(77.79, 74.77) * mm]});
            skSolve(sketch);
        }
        {
            var Q0;
            Q0=makeQuery(id+"F2.imprint","IMPRINT",FACE,{"disambiguationData":[TD([[makeQuery(id+"F2.imprint","IMPRINT",EDGE,{"derivedFrom":sQuery(id+"F2.wireOp",EDGE,"E49")}),1.0]])]});
            extrude(context, id + "F3", {"entities" : qUnion([Q0]), "depth" : 12.7 * mm, "offsetDistance" : 25.4 * mm});
        }
    });
